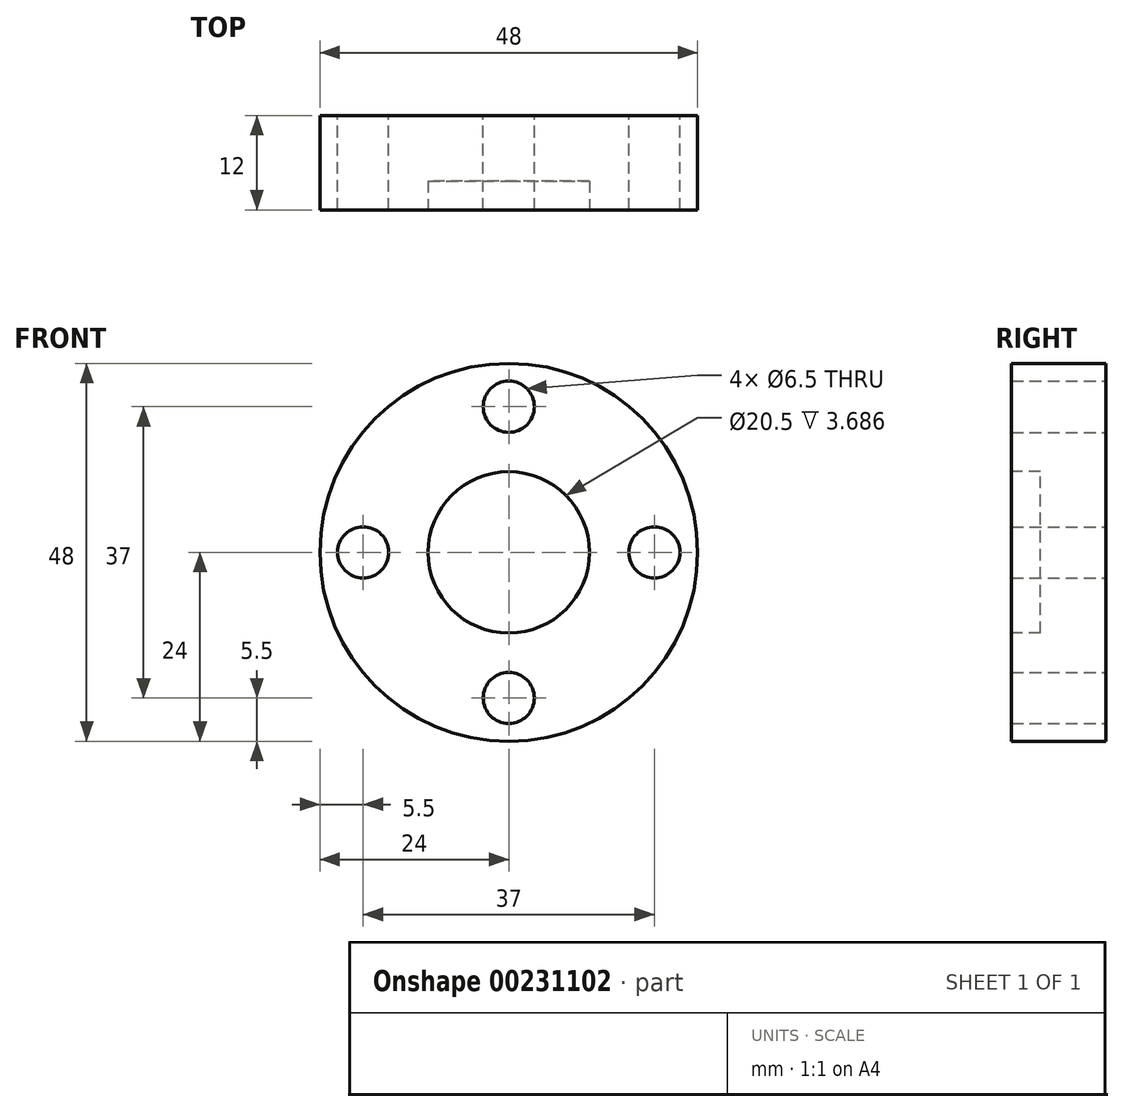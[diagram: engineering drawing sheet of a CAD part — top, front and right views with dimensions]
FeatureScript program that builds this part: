
annotation { "Feature Type Name" : "Feature", "Feature Type Description" : "" }
export const myFeature = defineFeature(function(context is Context, id is Id, definition is map)
    precondition{}
    {
        {
            var Q0;
            Q0=qCreatedBy(makeId("Right.planeOp"),FACE);
            var sketch = newSketch(context, id + "F0", { "sketchPlane" : qUnion([Q0])});
            skLineSegment(sketch, "E0.bottom", {"start": v(3.69, 0) * mm, "end": v(12, 0) * mm});
            skLineSegment(sketch, "E0.top", {"start": v(0, 24) * mm, "end": v(12, 24) * mm});
            skLineSegment(sketch, "E0.left", {"start": v(0, 10.25) * mm, "end": v(0, 24) * mm});
            skLineSegment(sketch, "E0.right", {"start": v(12, 0) * mm, "end": v(12, 24) * mm});
            skLineSegment(sketch, "E1", {"start": v(0, 10.25) * mm, "end": v(3.69, 10.25) * mm});
            skLineSegment(sketch, "E2", {"start": v(3.69, 10.25) * mm, "end": v(3.69, 0) * mm});
            skSolve(sketch);
        }
        {
            var Q0;
            Q0=makeQuery(id+"F0.imprint","IMPRINT",FACE,{"disambiguationData":[TD([[makeQuery(id+"F0.imprint","IMPRINT",EDGE,{"derivedFrom":sQuery(id+"F0.wireOp",EDGE,"E0.bottom")}),1.0]])]});
            var Q1;
            Q1=sQuery(id+"F0.wireOp",EDGE,"E0.bottom");
            revolve(context, id + "F1", {"entities" : qUnion([Q0]), "axis" : qUnion([Q1]), "revolveType" : RevolveType.FULL});
        }
        {
            var Q0;
            Q0=makeQuery(id+"F1.opRevolve","SWEPT_FACE",FACE,{"disambiguationData":[OSD([sQuery(id+"F0.wireOp",EDGE,"E0.right")])]});
            var sketch = newSketch(context, id + "F2", { "sketchPlane" : qUnion([Q0])});
            skCircle(sketch, "E3", {"center": v(0, 0) * mm, "radius": 18.5 * mm});
            skPoint(sketch, "E4", {"position": v(0, 18.5) * mm});
            skPoint(sketch, "E5", {"position": v(-18.5, 0) * mm});
            skPoint(sketch, "E6", {"position": v(18.5, 0) * mm});
            skPoint(sketch, "E7", {"position": v(0, -18.5) * mm});
            skSolve(sketch);
        }
        {
            var Q0;
            Q0=sQuery(id+"F2.wireOp",VERTEX,"E4");
            var Q1;
            Q1=sQuery(id+"F2.wireOp",VERTEX,"E5");
            var Q2;
            Q2=sQuery(id+"F2.wireOp",VERTEX,"E7");
            var Q3;
            Q3=sQuery(id+"F2.wireOp",VERTEX,"E6");
            var Q4;
            Q4=makeQuery(id+"F1.opRevolve","SWEPT_BODY",BODY,{"disambiguationData":[OSD([sQuery(id+"F0.wireOp",EDGE,"E0.bottom"),sQuery(id+"F0.wireOp",EDGE,"E0.top"),sQuery(id+"F0.wireOp",EDGE,"E0.left"),sQuery(id+"F0.wireOp",EDGE,"E0.right"),sQuery(id+"F0.wireOp",EDGE,"E1"),sQuery(id+"F0.wireOp",EDGE,"E2")])]});
            hole(context, id + "F3", {"style" : HoleStyle.SIMPLE, "endStyle" : HoleEndStyle.THROUGH, "holeDiameter" : 6.5 * mm, "startFromSketch" : true, "locations" : qUnion([Q0, Q1, Q2, Q3]), "scope" : qUnion([Q4]), "isTappedThrough" : true});
        }
    });
